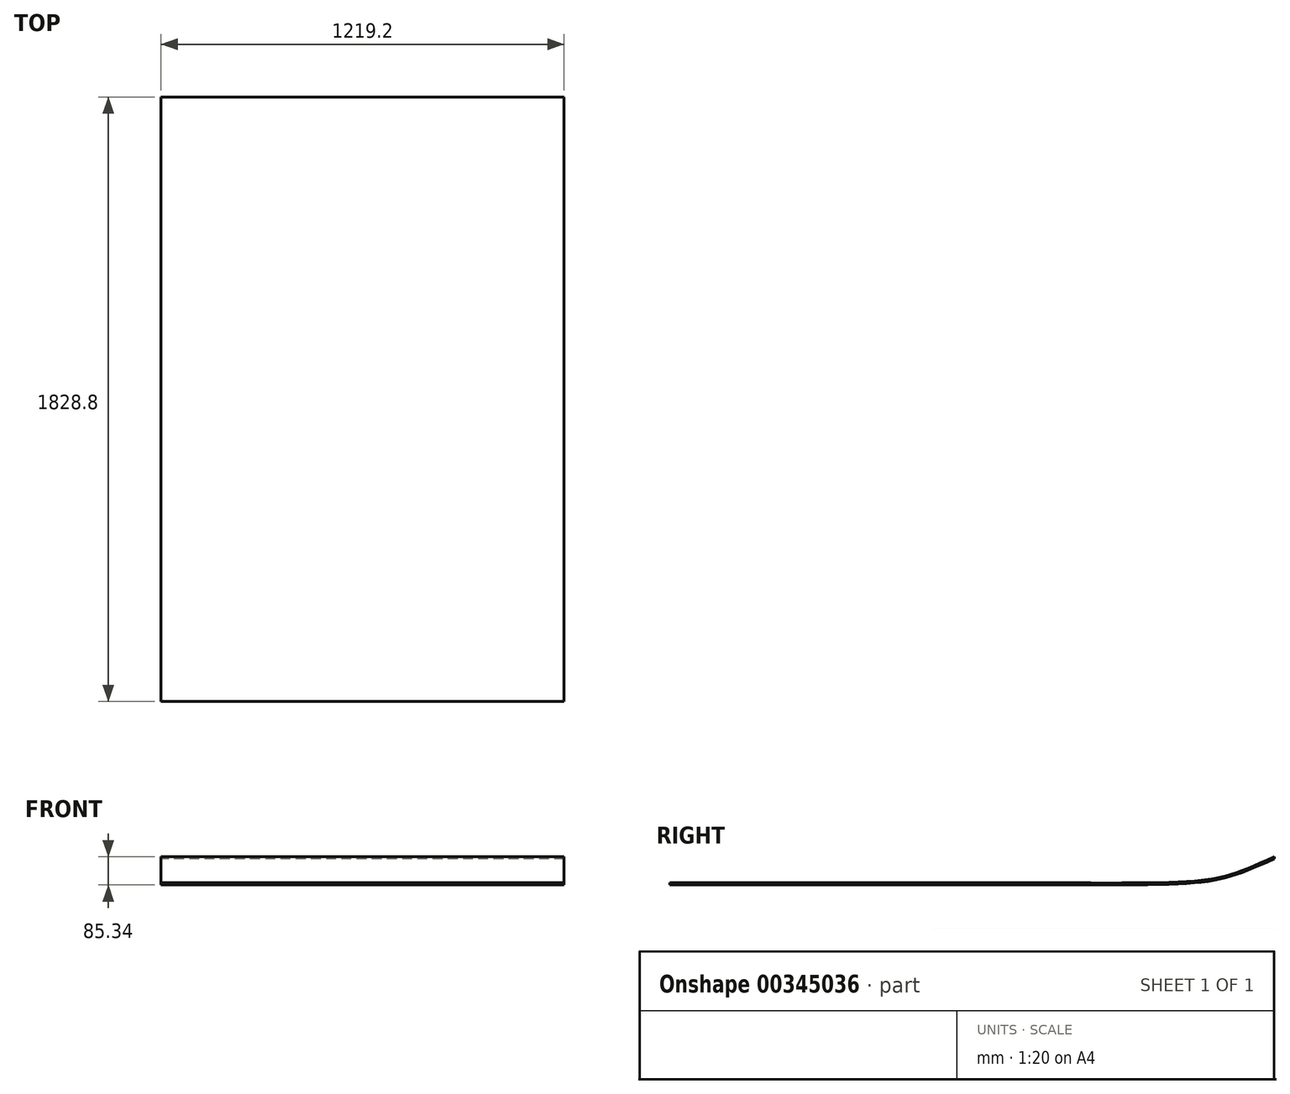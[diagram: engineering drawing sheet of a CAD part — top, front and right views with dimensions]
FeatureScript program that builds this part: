
annotation { "Feature Type Name" : "Feature", "Feature Type Description" : "" }
export const myFeature = defineFeature(function(context is Context, id is Id, definition is map)
    precondition{}
    {
        {
            var Q0;
            Q0=qCreatedBy(makeId("Right.planeOp"),FACE);
            var sketch = newSketch(context, id + "F0", { "sketchPlane" : qUnion([Q0])});
            skLineSegment(sketch, "E0", {"start": v(-1219.2, 0) * mm, "end": v(0, 0) * mm});
            skFitSpline(sketch, "E1", {"points": [v(0, 0) * mm, v(609.6, 79) * mm], "startDerivative": vector(1290.12, 0) * mm, "endDerivative": vector(538.68, 236.98) * mm});
            skLineSegment(sketch, "E2", {"start": v(-1219.2, 0) * mm, "end": v(-1219.2, 6.35) * mm});
            skLineSegment(sketch, "E3", {"start": v(-1219.2, 6.35) * mm, "end": v(0, 6.35) * mm});
            skLineSegment(sketch, "E4", {"start": v(609.6, 79) * mm, "end": v(609.6, 85.34) * mm});
            skFitSpline(sketch, "E5", {"points": [v(0, 6.35) * mm, v(609.6, 85.34) * mm], "startDerivative": vector(1290.12, -3) * mm, "endDerivative": vector(538.68, 239.97) * mm});
            skSolve(sketch);
        }
        {
            var Q0;
            Q0 = qSketchRegion(id + "F0", true);
            extrude(context, id + "F1", {"entities" : qUnion([Q0]), "depth" : 1219.2 * mm});
        }
    });
